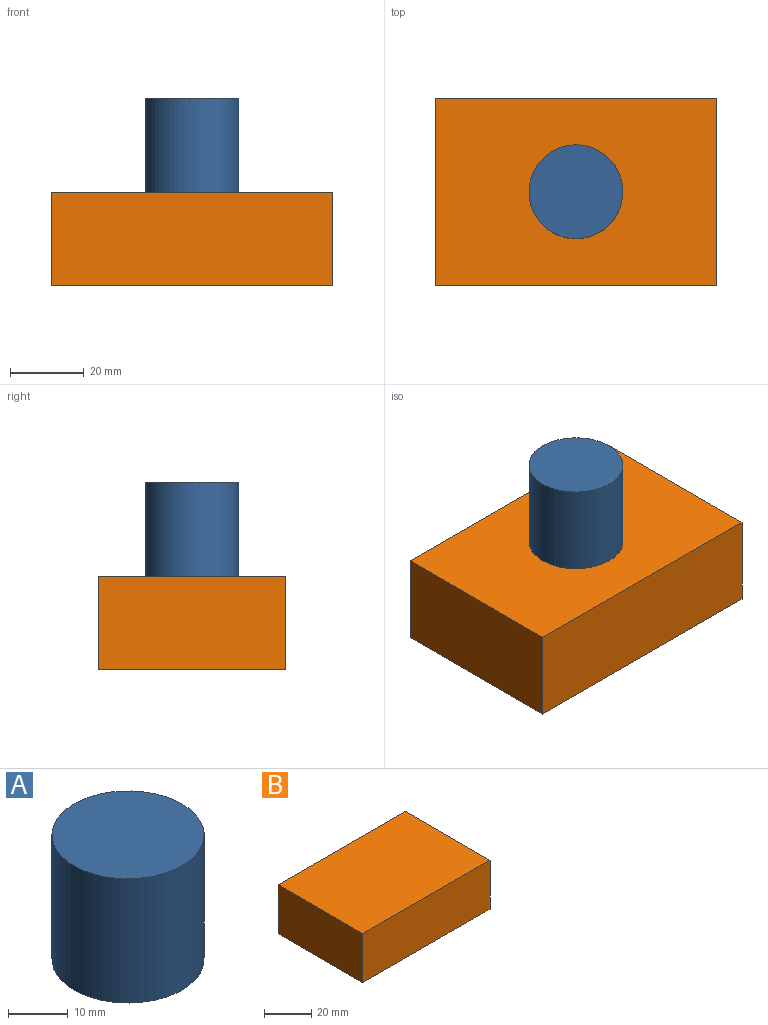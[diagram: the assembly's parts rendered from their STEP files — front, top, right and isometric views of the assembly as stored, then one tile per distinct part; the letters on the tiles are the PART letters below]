
ASSEMBLY  parts=2 mates=1
PART A: 3 faces, bbox 25.4x25.4x25.4 mm
  f0: cylinder r=12.7mm len=25.4mm, axis (0,0,-1), area 2026.8mm2, adj f1,f2
  f1: plane 25.4x25.4mm, normal (0,0,1), area 506.7mm2, adj f0
  f2: plane 25.4x25.4mm, normal (0,0,-1), area 506.7mm2, adj f0
PART B: 6 faces, bbox 76.2x50.8x25.4 mm
  f0: plane 76.2x25.4mm, normal (0,1,0), area 1935.5mm2, adj f1,f3,f4,f5
  f1: plane 50.8x25.4mm, normal (-1,0,0), area 1290.3mm2, adj f0,f2,f4,f5
  f2: plane 76.2x25.4mm, normal (0,-1,0), area 1935.5mm2, adj f1,f3,f4,f5
  f3: plane 50.8x25.4mm, normal (1,0,0), area 1290.3mm2, adj f0,f2,f4,f5
  f4: plane 76.2x50.8mm, normal (0,0,1), area 3871mm2, adj f0,f1,f2,f3
  f5: plane 76.2x50.8mm, normal (0,0,-1), area 3871mm2, adj f0,f1,f2,f3
PLACE A t=(-22.94,-5.14,-0.55)mm
PLACE B t=(-22.94,-5.14,-25.95)mm
MATE planar B.f4 <-> A.f0  axis (0,0,1) through (-22.94,-5.14,-0.55)mm
